# Revit family: Sink-Wall_Mount-Lavatory-KOHLER-ModernLife-K-77767K_1
name_source: partatom
category: Plumbing Fixtures
revit_build: Autodesk Revit 2017 (Build: 20160225_1515(x64)
units: mm (PartAtom-declared; Revit-internal decimal feet)

## family parameters
Cut with Voids When Loaded = No
Host = Face
OmniClass Number = 23.31.13.00
OmniClass Title = Sinks
Part Type = Normal
Room Calculation Point = No
Round Connector Dimension = Use Diameter
Shared = No

## types (3) — shared parameters
ADA Compliant = No
Assembly Code = D2010400
CW Connection = No
Cold Water Inlet = Cold Water Inlet
Date Modified = 08/24/2020
Default Elevation = 36"
Drain Included = No
Finish = Kohler-Vitreous_China-0-White
HW Connection = No
Height = 8 11/16"
Hot Water Inlet = Hot Water Inlet
Length = 21 5/8"
Manufacturer = KOHLER Co.
Master Format 2014 = 22 41 16
Master Format 2014 Name = Residential Lavatories and Sinks
Material = Vitreous china
Product Documentation Link = http://resources.kohler.com
Product Name = ModernLife
Product Page URL = https://www.kohlerasiapacific.com
URL = https://www.kohlerasiapacific.com
Vent Connection = No
Waste Connection = Yes
Waste Water Outlet = Waste Water Outlet
WaterSense Certified = No
Width = 17 11/16"

## per-type parameters (varying)
| type | 8 Inch Faucet Hole | Description | Faucet Hole Spacing | Model | Single Faucet Hole | Type |
| No Faucet Hole, 0-White | No | Wall-hung Lavatory | 0" | K-77767K-0 | No | 1 |
| Single Faucet Hole, 0-White | No | Wall-hung Lavatory with single faucet hole | 0" | K-77767K-1-0 | Yes | 2 |
| 8 Inch Faucet Hole, 0-White | Yes | Wall-hung Lavatory 8 inch widepread faucet holes | 8" | K-77767K-8-0 | Yes | 3 |

## geometry (parser evidence)
native form markers: Sweep x5
no freeform markers — native parametric forms only
